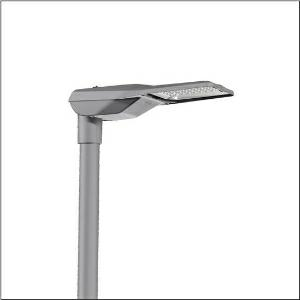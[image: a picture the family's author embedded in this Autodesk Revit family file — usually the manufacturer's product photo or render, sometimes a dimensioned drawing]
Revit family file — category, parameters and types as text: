
# Revit family: streetlight_sl_21_mini___p1_0a_5xe2a43s08hb_0f60
name_source: partatom
category: Lighting Fixtures
units: mm (PartAtom-declared; Revit-internal decimal feet)

## family parameters
Cut with Voids When Loaded = No
Host = Face
Light Source = No
Part Type = Normal
Room Calculation Point = No
Round Connector Dimension = Use Diameter
Shared = No

## types (1)
- --- (1 x LED, 9430 lm, 66 W, 4000K)
    Apparent Load = 66 VA
    CIE Flux Codes = 21 50 90 100 100
    Color Rendering = 70
    Color Temperature = 4000K
    Default Elevation = 1800 mm
    Description = Streetlight SL 21 mini, mast luminaire, primary light control with lens, of PMMA, primary optical cover: cover, of toughened safety glass, transparent, light distribution: P1.0a, light emission: direct distribution, primary light characteristic: asymmetric, installation type: side-entry, post-top, LED, High Power LED, rated luminous flux: 9.430lm, luminous efficacy: 143lm/W, light colour: 740, colour temperature: 4000K, control gear: D4i, control: overheat protection, constant luminous flux control, time-dependent luminous flux control, flexible luminous flux parameterisation, pre-setting: logarithmic dimming characteristic, mains connection: 220..240V, AC, 50/60Hz, start of lifetime: 66W, end of service life: 69W, reduction: 30W, luminaire housing, of diecast aluminium, powder-coated, Siteco® metallic grey (DB 702S), corrosivity category C5 mid according to DIN EN ISO 12944, please order mast flange separately, inclination adjustable: 0°, 5°, 10°, 15°, sealing non-destructively replaceable, multi-level sealing system, length: 628mm, width: 235mm, height: 110mm, mast flange for spigot size: 42mm (side-entry): 5XC10008XM4, 60/48mm (side-entry/post-top): 5XC10108XM2, 76/60mm (side-entry/post-top): 5XC10108XM1, mounting height: 4..8m, Smart Interface above, protection rating (complete): IP66, insulation class (complete): insulation class II (safety insulation), certification: CE, ENEC, ENEC+, VDE, impact resistance: IK10, permissible operating ambient temperature for outdoor applications: -40..+50°C, standard-compliant lighting for roads and squares, packaging unit: 1 piece

Light Distribution: P1.0a
    Height = 110 mm
    Lamp = 1 x LED
    Lamp Light Flux = 9430 lm
    Lamp Power = 66 W
    Lamp count = 1
    Length = 625 mm
    Luminous efficacy = 143 lm/W
    Manufacturer = Siteco
    ModVariant = No
    Model = 5XE2A43S08HB
    Number of Poles = 1
    OnlyDefault = Yes
    Power Factor = 1
    Product Name = Streetlight SL 21 mini | P1.0a
    Product group = mast luminaire | pylon top
    ProductGroupID = 6100
    Protection Class = Protection class II
    Protection Degree = IP 66
    RLX_Detail_Level = 1
    RLX_Emergency_Light_Flux = 0 lm
    RLX_Emergency_Type = 0
    RLX_Emergency_Type_DB = No
    RlxData = <blob elided: 37365 chars, md5=f5978a85>
    Socket = socket
    Standby Power = 0 W
    System Light Flux = 9430 lm
    System Power = 66 W
    Type Comments = factory setting: luminous flux: 100 % | dim-lin: 254 | 670 mA
    Type Image = l_1003515.jpg
    URL = http://relux.com
    VarID = @adj_207891
    Voltage = 0 V
    Weight = 0.00 kg
    Width = 234 mm

## geometry (parser evidence)
native form markers: Blend x4, Sweep x10
no freeform markers — native parametric forms only
